# Revit family: Lighting-Floodlight-Current-EXO-LSP-RGBW-White
name_source: partatom
category: Lighting Fixtures
units: mm (PartAtom-declared; Revit-internal decimal feet)

## family parameters
Cut with Voids When Loaded = No
Host = Face
Light Source = Yes
OmniClass Number = 23.80.70.11.14.17
OmniClass Title = Direct/Indirect
Part Type = Normal
Room Calculation Point = No
Round Connector Dimension = Use Diameter
Shared = Yes

## types (1)
- Lighting-Floodlight-Current-EXO-LSP-RGBW-White
    Additional Material Finish = Paint - Current - Matte White
    Apparent Load = 17 W
    Assembly Code = D5020200
    Available Finish Options = Available in Dark bronze finish
    Certifications = Listed to UL1598 for use in wet locations, FCC Title 47 Part 1, IP66
    Color Filter = 16777215
    Color Rendering Index = 70 CRI
    Default Elevation = 48 "
    Description = Lightscaper LSP-RGBW Series - FloodLight
    Dimming Lamp Color Temperature Shift = <None>
    Distribution Patterns = Wide (7X6)
    Features = Architectural Form Factor perfect for illuminating signage, building façade 
or landscapes
•  Manual Switching RGBW with 10-colors
•  Wide 7x6 distribution
•  Standard Knuckle Mount 
•  120-277 Volt
•  Standard Bronze Finish
•  Low Wattage, Low Lumen Flood
    Housing Material = Metal - Current - Dark Bronze
    Keynote = 16500
    Lamp = LED
    Lens Material Finish = Glass - Current - White
    Load Classification = Lighting
    Manufacturer = Current Lighting
    Model = Lightscaper LSP-RGBW Series - FloodLight
    Mounting = Please Refer to the Product Spec Sheet for Mounting Options
    No of Poles = 1
    Photometric Web File = LSP-RGBW White.IES
    Photometry Note = Please load ies file listed under Photometric Web File for accurate rendering.
    Power Factor = 0.9
    Tilt Angle = 90.00°
    Type Comments = Flood Light
    URL = www.currentlighting.com
    Version = 2021 V 1.2
    Voltage = 120 V
    Voltage Comments = Universal Voltage 120V-277V
    Warranty = 5 year limited
    Wattage Comments = 17W

## geometry (parser evidence)
native form markers: Sweep x3
no freeform markers — native parametric forms only
